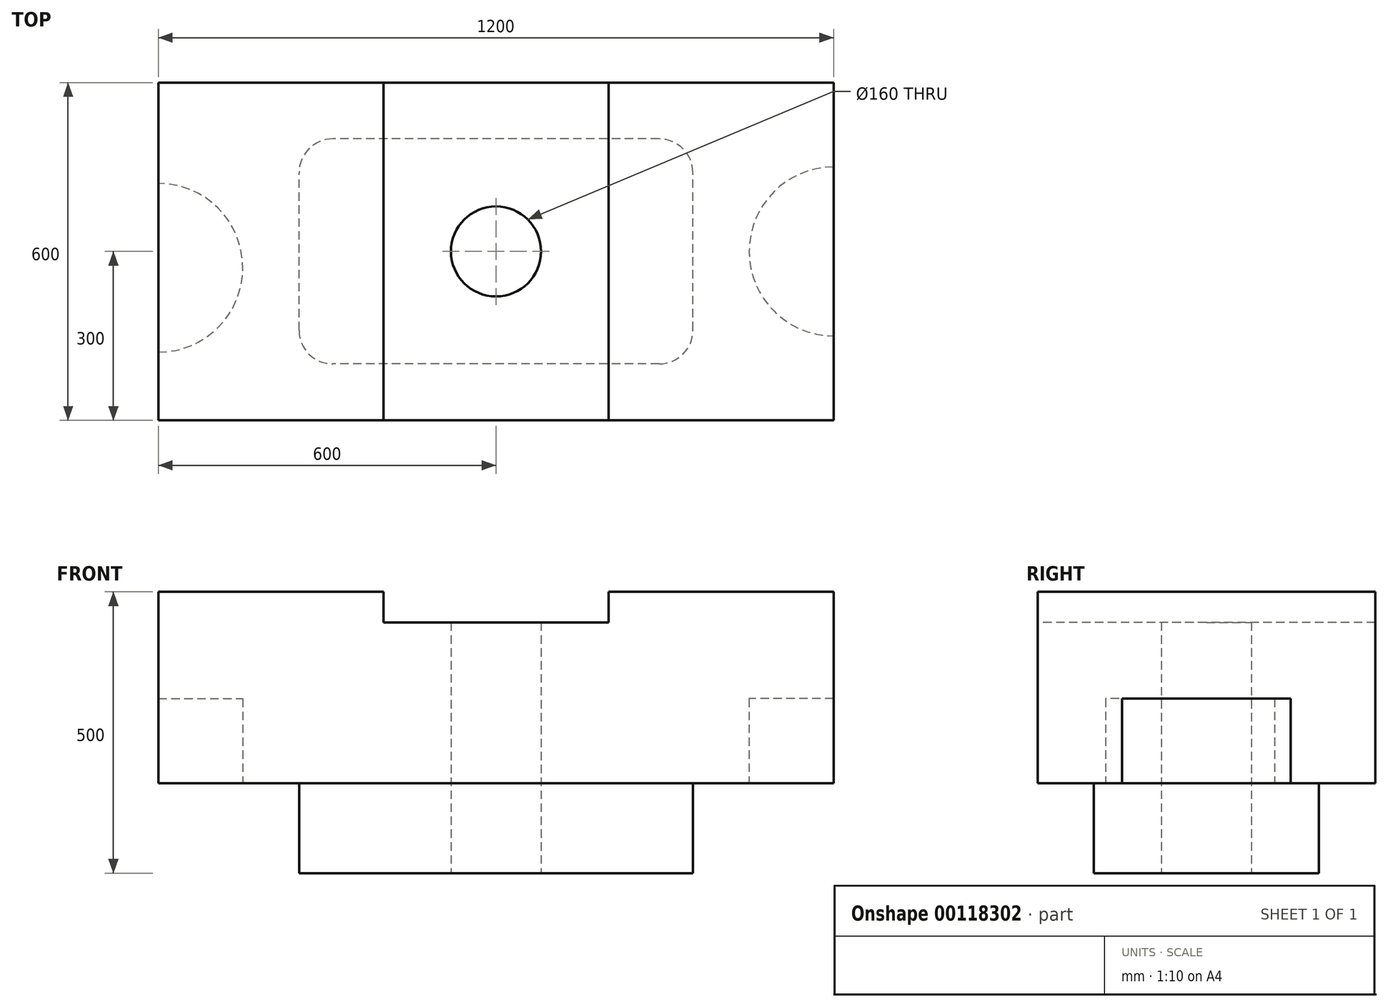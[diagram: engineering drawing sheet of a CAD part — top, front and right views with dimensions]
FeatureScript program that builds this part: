
annotation { "Feature Type Name" : "Feature", "Feature Type Description" : "" }
export const myFeature = defineFeature(function(context is Context, id is Id, definition is map)
    precondition{}
    {
        {
            var Q0;
            Q0=qCreatedBy(makeId("Top.planeOp"),FACE);
            var sketch = newSketch(context, id + "F0", { "sketchPlane" : qUnion([Q0])});
            skLineSegment(sketch, "E0.bottom", {"start": v(600, 300) * mm, "end": v(-600, 300) * mm});
            skLineSegment(sketch, "E0.top", {"start": v(600, -300) * mm, "end": v(-600, -300) * mm});
            skLineSegment(sketch, "E0.left", {"start": v(600, 300) * mm, "end": v(600, -300) * mm});
            skLineSegment(sketch, "E0.right", {"start": v(-600, 300) * mm, "end": v(-600, -300) * mm});
            skPoint(sketch, "E0.middle", {"position": v(0, 0) * mm});
            skSolve(sketch);
        }
        {
            var Q0;
            Q0 = qSketchRegion(id + "F0", true);
            extrude(context, id + "F1", {"entities" : qUnion([Q0]), "depth" : 340 * mm});
        }
        {
            var Q0;
            Q0=makeQuery(id+"F1.opExtrude","SWEPT_FACE",FACE,{"disambiguationData":[OSD([sQuery(id+"F0.wireOp",EDGE,"E0.top")])]});
            var sketch = newSketch(context, id + "F2", { "sketchPlane" : qUnion([Q0])});
            skLineSegment(sketch, "E1.bottom", {"start": v(200, 340) * mm, "end": v(-200, 340) * mm});
            skLineSegment(sketch, "E1.top", {"start": v(200, 285.73) * mm, "end": v(-200, 285.73) * mm});
            skLineSegment(sketch, "E1.left", {"start": v(200, 340) * mm, "end": v(200, 285.73) * mm});
            skLineSegment(sketch, "E1.right", {"start": v(-200, 340) * mm, "end": v(-200, 285.73) * mm});
            skSolve(sketch);
        }
        {
            var Q0;
            Q0 = qSketchRegion(id + "F2", true);
            extrude(context, id + "F3", {"entities" : qUnion([Q0]), "operationType" : NewBodyOperationType.REMOVE, "oppositeDirection" : true, "depth" : 600 * mm});
        }
        {
            var Q0;
            Q0=makeQuery(id+"F1.opExtrude","CAP_FACE",FACE,{"disambiguationData":[OSD([sQuery(id+"F0.wireOp",EDGE,"E0.bottom"),sQuery(id+"F0.wireOp",EDGE,"E0.top"),sQuery(id+"F0.wireOp",EDGE,"E0.left"),sQuery(id+"F0.wireOp",EDGE,"E0.right")])],"isStart":true});
            var sketch = newSketch(context, id + "F4", { "sketchPlane" : qUnion([Q0])});
            skLineSegment(sketch, "E2.bottom", {"start": v(350, 200) * mm, "end": v(-350, 200) * mm});
            skLineSegment(sketch, "E2.top", {"start": v(350, -200) * mm, "end": v(-350, -200) * mm});
            skLineSegment(sketch, "E2.left", {"start": v(350, 200) * mm, "end": v(350, -200) * mm});
            skLineSegment(sketch, "E2.right", {"start": v(-350, 200) * mm, "end": v(-350, -200) * mm});
            skPoint(sketch, "E2.middle", {"position": v(0, 0) * mm});
            skSolve(sketch);
        }
        {
            var Q0;
            Q0=makeQuery(id+"F4.imprint","IMPRINT",FACE,{"disambiguationData":[TD([[makeQuery(id+"F4.imprint","IMPRINT",EDGE,{"derivedFrom":sQuery(id+"F4.wireOp",EDGE,"E2.bottom")}),1.0]])]});
            extrude(context, id + "F5", {"entities" : qUnion([Q0]), "operationType" : NewBodyOperationType.ADD, "depth" : 160 * mm});
        }
        {
            var Q0;
            Q0=makeQuery(id+"F5.opExtrude","CAP_FACE",FACE,{"disambiguationData":[OSD([sQuery(id+"F4.wireOp",EDGE,"E2.bottom"),sQuery(id+"F4.wireOp",EDGE,"E2.top"),sQuery(id+"F4.wireOp",EDGE,"E2.left"),sQuery(id+"F4.wireOp",EDGE,"E2.right")])],"isStart":false});
            var sketch = newSketch(context, id + "F6", { "sketchPlane" : qUnion([Q0])});
            skCircle(sketch, "E3", {"center": v(0, 0) * mm, "radius": 80 * mm});
            skSolve(sketch);
        }
        {
            var Q0;
            Q0=makeQuery(id+"F6.imprint","IMPRINT",FACE,{"disambiguationData":[TD([[makeQuery(id+"F6.imprint","IMPRINT",EDGE,{"derivedFrom":sQuery(id+"F6.wireOp",EDGE,"E3")}),1.0]])]});
            extrude(context, id + "F7", {"entities" : qUnion([Q0]), "operationType" : NewBodyOperationType.REMOVE, "endBound" : BoundingType.THROUGH_ALL, "oppositeDirection" : true, "depth" : 25 * mm});
        }
        {
            var Q0;
            Q0=makeQuery(id+"F1.opExtrude","CAP_FACE",FACE,{"disambiguationData":[OSD([sQuery(id+"F0.wireOp",EDGE,"E0.bottom"),sQuery(id+"F0.wireOp",EDGE,"E0.top"),sQuery(id+"F0.wireOp",EDGE,"E0.left"),sQuery(id+"F0.wireOp",EDGE,"E0.right")])],"isStart":true});
            var sketch = newSketch(context, id + "F8", { "sketchPlane" : qUnion([Q0])});
            skCircle(sketch, "E4", {"center": v(-600, 29.04) * mm, "radius": 150 * mm});
            skCircle(sketch, "E5", {"center": v(600, 0) * mm, "radius": 150 * mm});
            skSolve(sketch);
        }
        {
            var Q0;
            {var subQ0=sQuery(id+"F8.wireOp",EDGE,"E5");var subQ1=makeQuery(id+"F1.opExtrude","CAP_EDGE",EDGE,{"disambiguationData":[OSD([sQuery(id+"F0.wireOp",EDGE,"E0.left")])],"isStart":true});var subQ2=makeQuery(id+"F8.imprint","INTERSECT",VERTEX,{"disambiguationData":[OD(0.0)],"derivedFrom":[subQ1,subQ0]});Q0=makeQuery(id+"F8.imprint","IMPRINT",FACE,{"disambiguationData":[TD([[makeQuery(id+"F8.imprint","IMPRINT",EDGE,{"disambiguationData":[TD([[subQ2,1.0]])],"derivedFrom":subQ0}),1.0]])]});}
            extrude(context, id + "F9", {"entities" : qUnion([Q0]), "operationType" : NewBodyOperationType.REMOVE, "oppositeDirection" : true, "depth" : 150 * mm});
        }
        {
            var Q0;
            Q0=makeQuery(id+"F5.opExtrude","SWEPT_EDGE",EDGE,{"disambiguationData":[OSD([sQuery(id+"F4.wireOp",EDGE,"E2.top"),sQuery(id+"F4.wireOp",EDGE,"E2.right")])]});
            var Q1;
            Q1=makeQuery(id+"F5.opExtrude","SWEPT_EDGE",EDGE,{"disambiguationData":[OSD([sQuery(id+"F4.wireOp",EDGE,"E2.top"),sQuery(id+"F4.wireOp",EDGE,"E2.left")])]});
            var Q2;
            Q2=makeQuery(id+"F5.opExtrude","SWEPT_EDGE",EDGE,{"disambiguationData":[OSD([sQuery(id+"F4.wireOp",EDGE,"E2.bottom"),sQuery(id+"F4.wireOp",EDGE,"E2.left")])]});
            var Q3;
            Q3=makeQuery(id+"F5.opExtrude","SWEPT_EDGE",EDGE,{"disambiguationData":[OSD([sQuery(id+"F4.wireOp",EDGE,"E2.bottom"),sQuery(id+"F4.wireOp",EDGE,"E2.right")])]});
            fillet(context, id + "F10", {"entities" : qUnion([Q0, Q1, Q2, Q3]), "radius" : 60 * mm, "tangentPropagation" : true, "allowEdgeOverflow" : false});
        }
        {
            var Q0;
            {var subQ0=sQuery(id+"F8.wireOp",EDGE,"E4");var subQ1=makeQuery(id+"F1.opExtrude","CAP_EDGE",EDGE,{"disambiguationData":[OSD([sQuery(id+"F0.wireOp",EDGE,"E0.right")])],"isStart":true});var subQ2=makeQuery(id+"F8.imprint","INTERSECT",VERTEX,{"disambiguationData":[OD(0.0)],"derivedFrom":[subQ1,subQ0]});Q0=makeQuery(id+"F8.imprint","IMPRINT",FACE,{"disambiguationData":[TD([[makeQuery(id+"F8.imprint","IMPRINT",EDGE,{"disambiguationData":[TD([[subQ2,-1.0]])],"derivedFrom":subQ0}),1.0]])]});}
            extrude(context, id + "F11", {"entities" : qUnion([Q0]), "operationType" : NewBodyOperationType.REMOVE, "oppositeDirection" : true, "depth" : 150 * mm});
        }
    });
